# Revit family: Vents_VKM_Eng
name_source: partatom
category: Mechanical Equipment
units: mm (PartAtom-declared; Revit-internal decimal feet)

## family parameters
Always vertical = Yes
Classification = None
Cut with Voids When Loaded = No
Part Type = Normal
Room Calculation Point = No
Round Connector Dimension = Use Diameter
Shared = No
Work Plane-Based = No

## types (17) — shared parameters
00_20_Manufacturer = Vents
00_20_Name = Inline centrifugal fan
Casing Material = Metal, painted, blue, matte RAL 5007
Frequency = 50 Hz
Load Classification = HVAC
Maintenance zone material = <By Category>
Manufacturer = Vents
Number of Fase = 1
URL = https://ventilation-system.com
Voltage = 230 V
zero-valued in all types: Default Elevation

## per-type parameters (varying)
- VKM 100 Q: Amperage=0 A; Apparent Load=55 VA; B=310 mm; B1=270 mm; B2=190 mm; D1=255 mm; D2=230 mm; Diameter=100 mm  [stored 0.328084 ft]; Dy=100 mm  [stored 0.328084 ft]; Fastening=Fastening : VKM 100 Q; Fastening_1=Yes; Fastening_2=No; H1=178 mm; Height=305 mm; L=205 mm; L1=20 mm  [stored 0.0656168 ft]; L2=25 mm  [stored 0.082021 ft]; L3=30 mm  [stored 0.0984252 ft]; L4=70 mm  [stored 0.229659 ft]; L5=48 mm  [stored 0.15748 ft]; L6=95 mm  [stored 0.31168 ft]; L7=40 mm  [stored 0.131234 ft]; L8=100 mm  [stored 0.328084 ft]; Length=205 mm; Maximum Air Flow=65.0 L/s; Motor=Motor : Motor_42 Вт; Power=45 W; R1=128 mm; R2=133 mm; Ry=50 mm  [stored 0.164042 ft]; Sound pressure level at 3 m distance=38 dBA; Weight=2.90 kg; Width=310 mm
- VKM 315: Amperage=1 A; Apparent Load=177 VA; B=455 mm; B1=415 mm; B2=335 mm; D1=405 mm; D2=380 mm; Diameter=315 mm; Dy=315 mm; Fastening=Fastening : VKMS 315; Fastening_1=Yes; Fastening_2=No; H1=253 mm; Height=455 mm; L=260 mm; L1=30 mm  [stored 0.0984252 ft]; L2=30 mm  [stored 0.0984252 ft]; L3=40 mm  [stored 0.131234 ft]; L4=77 mm  [stored 0.252625 ft]; L5=56 mm; L6=102 mm; L7=50 mm  [stored 0.164042 ft]; L8=107 mm  [stored 0.35105 ft]; Length=260 mm; Maximum Air Flow=400.0 L/s; Motor=Motor : Motor_42 Вт; Power=171 W; R1=203 mm; R2=208 mm; Ry=158 mm; Sound pressure level at 3 m distance=52 dBA; Weight=8.00 kg; Width=455 mm
- VKM 100: Amperage=0 A; Apparent Load=64 VA; B=310 mm; B1=270 mm; B2=190 mm; D1=255 mm; D2=230 mm; Diameter=100 mm  [stored 0.328084 ft]; Dy=100 mm  [stored 0.328084 ft]; Fastening=Fastening : VKM 100; Fastening_1=Yes; Fastening_2=No; H1=178 mm; Height=305 mm; L=205 mm; L1=20 mm  [stored 0.0656168 ft]; L2=25 mm  [stored 0.082021 ft]; L3=30 mm  [stored 0.0984252 ft]; L4=70 mm  [stored 0.229659 ft]; L5=48 mm  [stored 0.15748 ft]; L6=95 mm  [stored 0.31168 ft]; L7=40 mm  [stored 0.131234 ft]; L8=100 mm  [stored 0.328084 ft]; Length=205 mm; Maximum Air Flow=77.5 L/s; Motor=Motor : Motor_42 Вт; Power=60 W; R1=128 mm; R2=133 mm; Ry=50 mm  [stored 0.164042 ft]; Sound pressure level at 3 m distance=40 dBA; Weight=3.20 kg; Width=310 mm
- VKM 125 Q: Amperage=0 A; Apparent Load=58 VA; B=310 mm; B1=270 mm; B2=190 mm; D1=255 mm; D2=230 mm; Diameter=125 mm  [stored 0.410105 ft]; Dy=125 mm  [stored 0.410105 ft]; Fastening=Fastening : VKM 125 Q; Fastening_1=Yes; Fastening_2=No; H1=178 mm; Height=305 mm; L=205 mm; L1=20 mm  [stored 0.0656168 ft]; L2=25 mm  [stored 0.082021 ft]; L3=30 mm  [stored 0.0984252 ft]; L4=70 mm  [stored 0.229659 ft]; L5=48 mm  [stored 0.15748 ft]; L6=95 mm  [stored 0.31168 ft]; L7=40 mm  [stored 0.131234 ft]; L8=100 mm  [stored 0.328084 ft]; Length=205 mm; Maximum Air Flow=90.5 L/s; Motor=Motor : Motor_42 Вт; Power=47 W; R1=128 mm; R2=133 mm; Ry=63 mm  [stored 0.206693 ft]; Sound pressure level at 3 m distance=37 dBA; Weight=2.90 kg; Width=310 mm
- VKM 125: Amperage=0 A; Apparent Load=67 VA; B=310 mm; B1=270 mm; B2=190 mm; D1=255 mm; D2=230 mm; Diameter=125 mm  [stored 0.410105 ft]; Dy=125 mm  [stored 0.410105 ft]; Fastening=Fastening : VKM 125; Fastening_1=Yes; Fastening_2=No; H1=178 mm; Height=305 mm; L=205 mm; L1=20 mm  [stored 0.0656168 ft]; L2=25 mm  [stored 0.082021 ft]; L3=30 mm  [stored 0.0984252 ft]; L4=70 mm  [stored 0.229659 ft]; L5=48 mm  [stored 0.15748 ft]; L6=95 mm  [stored 0.31168 ft]; L7=40 mm  [stored 0.131234 ft]; L8=100 mm  [stored 0.328084 ft]; Length=205 mm; Maximum Air Flow=100.0 L/s; Motor=Motor : Motor_42 Вт; Power=64 W; R1=128 mm; R2=133 mm; Ry=63 mm  [stored 0.206693 ft]; Sound pressure level at 3 m distance=40 dBA; Weight=3.20 kg; Width=310 mm
- VKM 150: Amperage=0 A; Apparent Load=104 VA; B=395 mm; B1=355 mm; B2=275 mm; D1=345 mm; D2=320 mm; Diameter=150 mm  [stored 0.492126 ft]; Dy=150 mm  [stored 0.492126 ft]; Fastening=Fastening : VKM 150; Fastening_1=Yes; Fastening_2=No; H1=223 mm; Height=395 mm; L=200 mm; L1=20 mm  [stored 0.0656168 ft]; L2=20 mm  [stored 0.0656168 ft]; L3=40 mm  [stored 0.131234 ft]; L4=67 mm; L5=46 mm; L6=92 mm  [stored 0.301837 ft]; L7=50 mm  [stored 0.164042 ft]; L8=97 mm  [stored 0.318241 ft]; Length=200 mm; Maximum Air Flow=161.0 L/s; Motor=Motor : Motor_42 Вт; Power=100 W; R1=173 mm; R2=178 mm; Ry=75 mm  [stored 0.246063 ft]; Sound pressure level at 3 m distance=45 dBA; Weight=5.10 kg; Width=395 mm
- VKMS 150: Amperage=1 A; Apparent Load=127 VA; B=395 mm; B1=355 mm; B2=275 mm; D1=345 mm; D2=320 mm; Diameter=150 mm  [stored 0.492126 ft]; Dy=150 mm  [stored 0.492126 ft]; Fastening=Fastening : VKMS 150; Fastening_1=Yes; Fastening_2=No; H1=223 mm; Height=395 mm; L=230 mm; L1=20 mm  [stored 0.0656168 ft]; L2=20 mm  [stored 0.0656168 ft]; L3=40 mm  [stored 0.131234 ft]; L4=82 mm  [stored 0.269029 ft]; L5=61 mm; L6=107 mm  [stored 0.35105 ft]; L7=50 mm  [stored 0.164042 ft]; L8=112 mm  [stored 0.367454 ft]; Length=230 mm; Maximum Air Flow=197.0 L/s; Motor=Motor : Motor_42 Вт; Power=127 W; R1=173 mm; R2=178 mm; Ry=75 mm  [stored 0.246063 ft]; Sound pressure level at 3 m distance=48 dBA; Weight=5.60 kg; Width=395 mm
- VKM 160: Amperage=0 A; Apparent Load=101 VA; B=360 mm; B1=320 mm; B2=240 mm; D1=305 mm; D2=280 mm; Diameter=160 mm; Dy=160 mm; Fastening=Fastening : VKM 160; Fastening_1=Yes; Fastening_2=No; H1=203 mm; Height=355 mm; L=220 mm; L1=25 mm  [stored 0.082021 ft]; L2=25 mm  [stored 0.082021 ft]; L3=30 mm  [stored 0.0984252 ft]; L4=67 mm; L5=46 mm; L6=92 mm  [stored 0.301837 ft]; L7=40 mm  [stored 0.131234 ft]; L8=97 mm  [stored 0.318241 ft]; Length=220 mm; Maximum Air Flow=157.5 L/s; Motor=Motor : Motor_42 Вт; Power=99 W; R1=153 mm; R2=158 mm; Ry=80 mm  [stored 0.262467 ft]; Sound pressure level at 3 m distance=45 dBA; Weight=5.00 kg; Width=360 mm
- VKMS 200: Amperage=1 A; Apparent Load=193 VA; B=395 mm; B1=355 mm; B2=275 mm; D1=345 mm; D2=320 mm; Diameter=200 mm; Dy=200 mm; Fastening=Fastening : VKMS 200; Fastening_1=Yes; Fastening_2=No; H1=223 mm; Height=395 mm; L=255 mm; L1=25 mm  [stored 0.082021 ft]; L2=30 mm  [stored 0.0984252 ft]; L3=40 mm  [stored 0.131234 ft]; L4=85 mm  [stored 0.278871 ft]; L5=63 mm  [stored 0.206693 ft]; L6=110 mm  [stored 0.360892 ft]; L7=50 mm  [stored 0.164042 ft]; L8=115 mm  [stored 0.377297 ft]; Length=255 mm; Maximum Air Flow=319.5 L/s; Motor=Motor : Motor_42 Вт; Power=193 W; R1=173 mm; R2=178 mm; Ry=100 mm  [stored 0.328084 ft]; Sound pressure level at 3 m distance=49 dBA; Weight=8.30 kg; Width=395 mm
- VKM 250 E: Amperage=0 A; Apparent Load=108 VA; B=395 mm; B1=355 mm; B2=275 mm; D1=345 mm; D2=320 mm; Diameter=250 mm; Dy=250 mm; Fastening=Fastening : VKM 250 E; Fastening_1=Yes; Fastening_2=No; H1=223 mm; Height=395 mm; L=250 mm; L1=25 mm  [stored 0.082021 ft]; L2=30 mm  [stored 0.0984252 ft]; L3=40 mm  [stored 0.131234 ft]; L4=82 mm  [stored 0.269029 ft]; L5=61 mm; L6=107 mm  [stored 0.35105 ft]; L7=50 mm  [stored 0.164042 ft]; L8=112 mm  [stored 0.367454 ft]; Length=250 mm; Maximum Air Flow=250.0 L/s; Motor=Motor : Motor_42 Вт; Power=95 W; R1=173 mm; R2=178 mm; Ry=125 mm  [stored 0.410105 ft]; Sound pressure level at 3 m distance=47 dBA; Weight=6.20 kg; Width=395 mm
- VKM 250: Amperage=1 A; Apparent Load=196 VA; B=395 mm; B1=355 mm; B2=275 mm; D1=345 mm; D2=320 mm; Diameter=250 mm; Dy=250 mm; Fastening=Fastening : VKM 250; Fastening_1=Yes; Fastening_2=No; H1=223 mm; Height=395 mm; L=250 mm; L1=25 mm  [stored 0.082021 ft]; L2=30 mm  [stored 0.0984252 ft]; L3=40 mm  [stored 0.131234 ft]; L4=82 mm  [stored 0.269029 ft]; L5=61 mm; L6=107 mm  [stored 0.35105 ft]; L7=50 mm  [stored 0.164042 ft]; L8=112 mm  [stored 0.367454 ft]; Length=250 mm; Maximum Air Flow=394.5 L/s; Motor=Motor : Motor_42 Вт; Power=194 W; R1=173 mm; R2=178 mm; Ry=125 mm  [stored 0.410105 ft]; Sound pressure level at 3 m distance=50 dBA; Weight=8.40 kg; Width=395 mm
- VKMS 315: Amperage=1 A; Apparent Load=308 VA; B=455 mm; B1=415 mm; B2=335 mm; D1=405 mm; D2=380 mm; Diameter=315 mm; Dy=315 mm; Fastening=Fastening : VKMS 315; Fastening_1=Yes; Fastening_2=No; H1=253 mm; Height=455 mm; L=290 mm; L1=30 mm  [stored 0.0984252 ft]; L2=30 mm  [stored 0.0984252 ft]; L3=40 mm  [stored 0.131234 ft]; L4=92 mm  [stored 0.301837 ft]; L5=71 mm; L6=117 mm  [stored 0.383858 ft]; L7=50 mm  [stored 0.164042 ft]; L8=122 mm  [stored 0.400262 ft]; Length=290 mm; Maximum Air Flow=533.0 L/s; Motor=Motor : Motor_42 Вт; Power=295 W; R1=203 mm; R2=208 mm; Ry=158 mm; Sound pressure level at 3 m distance=54 dBA; Weight=8.80 kg; Width=455 mm
- VKM 200: Amperage=1 A; Apparent Load=136 VA; B=395 mm; B1=355 mm; B2=275 mm; D1=345 mm; D2=320 mm; Diameter=200 mm; Dy=200 mm; Fastening=Fastening : VKM 200; Fastening_1=Yes; Fastening_2=No; H1=223 mm; Height=395 mm; L=255 mm; L1=25 mm  [stored 0.082021 ft]; L2=30 mm  [stored 0.0984252 ft]; L3=40 mm  [stored 0.131234 ft]; L4=85 mm  [stored 0.278871 ft]; L5=63 mm  [stored 0.206693 ft]; L6=110 mm  [stored 0.360892 ft]; L7=50 mm  [stored 0.164042 ft]; L8=115 mm  [stored 0.377297 ft]; Length=255 mm; Maximum Air Flow=297.0 L/s; Motor=Motor : Motor_42 Вт; Power=135 W; R1=173 mm; R2=178 mm; Ry=100 mm  [stored 0.328084 ft]; Sound pressure level at 3 m distance=48 dBA; Weight=6.60 kg; Width=395 mm
- VKMS 160: Amperage=1 A; Apparent Load=122 VA; B=390 mm; B1=350 mm; B2=270 mm; D1=340 mm; D2=315 mm; Diameter=160 mm; Dy=160 mm; Fastening=Fastening : VKMS 160; Fastening_1=Yes; Fastening_2=No; H1=220 mm; Height=390 mm; L=245 mm; L1=25 mm  [stored 0.082021 ft]; L2=20 mm  [stored 0.0656168 ft]; L3=40 mm  [stored 0.131234 ft]; L4=80 mm  [stored 0.262467 ft]; L5=58 mm  [stored 0.190289 ft]; L6=105 mm; L7=50 mm  [stored 0.164042 ft]; L8=110 mm  [stored 0.360892 ft]; Length=245 mm; Maximum Air Flow=192.0 L/s; Motor=Motor : Motor_42 Вт; Power=121 W; R1=170 mm; R2=175 mm; Ry=80 mm  [stored 0.262467 ft]; Sound pressure level at 3 m distance=48 dBA; Weight=6.40 kg; Width=390 mm
- VKM 355 Q: Amperage=1 A; Apparent Load=244 VA; B=552 mm; B1=522 mm; B2=442 mm; D1=460 mm; D2=435 mm; Diameter=355 mm; Dy=355 mm; Fastening=Fastening : VKM 355 Q; Fastening_1=No; Fastening_2=Yes; H1=280 mm; Height=460 mm; L=506 mm; L1=60 mm  [stored 0.19685 ft]; L2=60 mm  [stored 0.19685 ft]; L3=70 mm  [stored 0.229659 ft]; L4=140 mm  [stored 0.459318 ft]; L5=75 mm  [stored 0.246063 ft]; L6=140 mm  [stored 0.459318 ft]; L7=90 mm  [stored 0.295276 ft]; L8=150 mm  [stored 0.492126 ft]; Length=506 mm; Maximum Air Flow=625.0 L/s; Motor=Motor : Motor_420 Вт; Power=233 W; R1=230 mm; R2=235 mm; Ry=178 mm; Sound pressure level at 3 m distance=58 dBA; Weight=18.80 kg; Width=552 mm
- VKM 400: Amperage=2 A; Apparent Load=513 VA; B=663 mm; B1=634 mm; B2=554 mm; D1=570 mm; D2=545 mm; Diameter=400 mm; Dy=400 mm; Fastening=Fastening : VKM 400; Fastening_1=No; Fastening_2=Yes; H1=335 mm; Height=570 mm; L=570 mm; L1=60 mm  [stored 0.19685 ft]; L2=60 mm  [stored 0.19685 ft]; L3=70 mm  [stored 0.229659 ft]; L4=172 mm; L5=75 mm  [stored 0.246063 ft]; L6=140 mm  [stored 0.459318 ft]; L7=90 mm  [stored 0.295276 ft]; L8=150 mm  [stored 0.492126 ft]; Length=570 mm; Maximum Air Flow=858.0 L/s; Motor=Motor : Motor_420 Вт; Power=460 W; R1=285 mm; R2=290 mm; Ry=200 mm; Sound pressure level at 3 m distance=61 dBA; Weight=25.10 kg; Width=663 mm
- VKM 450: Amperage=3 A; Apparent Load=665 VA; B=700 mm; B1=670 mm; B2=590 mm; D1=608 mm; D2=583 mm; Diameter=450 mm; Dy=450 mm; Fastening=Fastening : VKM 450; Fastening_1=No; Fastening_2=Yes; H1=354 mm; Height=608 mm; L=644 mm; L1=60 mm  [stored 0.19685 ft]; L2=60 mm  [stored 0.19685 ft]; L3=80 mm  [stored 0.262467 ft]; L4=209 mm; L5=75 mm  [stored 0.246063 ft]; L6=140 mm  [stored 0.459318 ft]; L7=100 mm  [stored 0.328084 ft]; L8=150 mm  [stored 0.492126 ft]; Length=644 mm; Maximum Air Flow=1472.0 L/s; Motor=Motor : Motor_420 Вт; Power=665 W; R1=304 mm; R2=309 mm; Ry=225 mm; Sound pressure level at 3 m distance=65 dBA; Weight=27.26 kg; Width=700 mm

note: column(s) folded — value = type name in every type: 00_20_Type

note: [stored X ft] marks values corroborated as IEEE doubles in the binary element streams (Revit-internal decimal feet)
